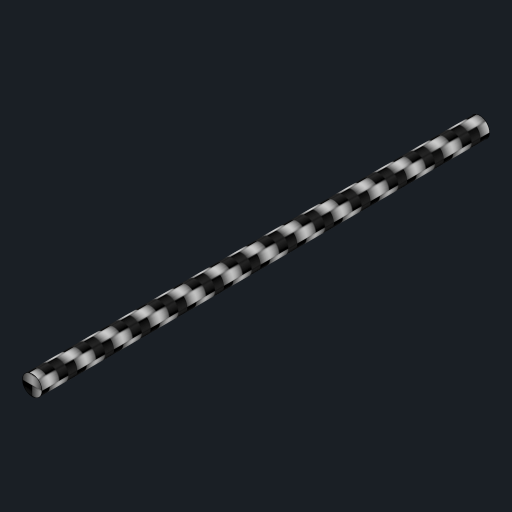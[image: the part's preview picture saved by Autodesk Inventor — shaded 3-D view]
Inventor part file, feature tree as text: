
AUTODESK INVENTOR PART (.ipt)
format: ipt  version: 2023 (Build 270158000, 158)  size: 107,008 bytes
history: native  units: in
note: dims shown in document units (in); Inventor stores cm internally (conversion verified against a paired STEP export)
features: other x1, extrude x1, sketch x1
ambient origin geometry x8: Origin, YZ Plane, XZ Plane, XY Plane, X Axis, Y Axis, Z Axis, Center Point
bodies: Body1 (feature_tree)
feature tree (3):
  other  "ソリッド1"
  extrude  "押し出し1"  Depth=0.0787in
  sketch  "スケッチ1"
